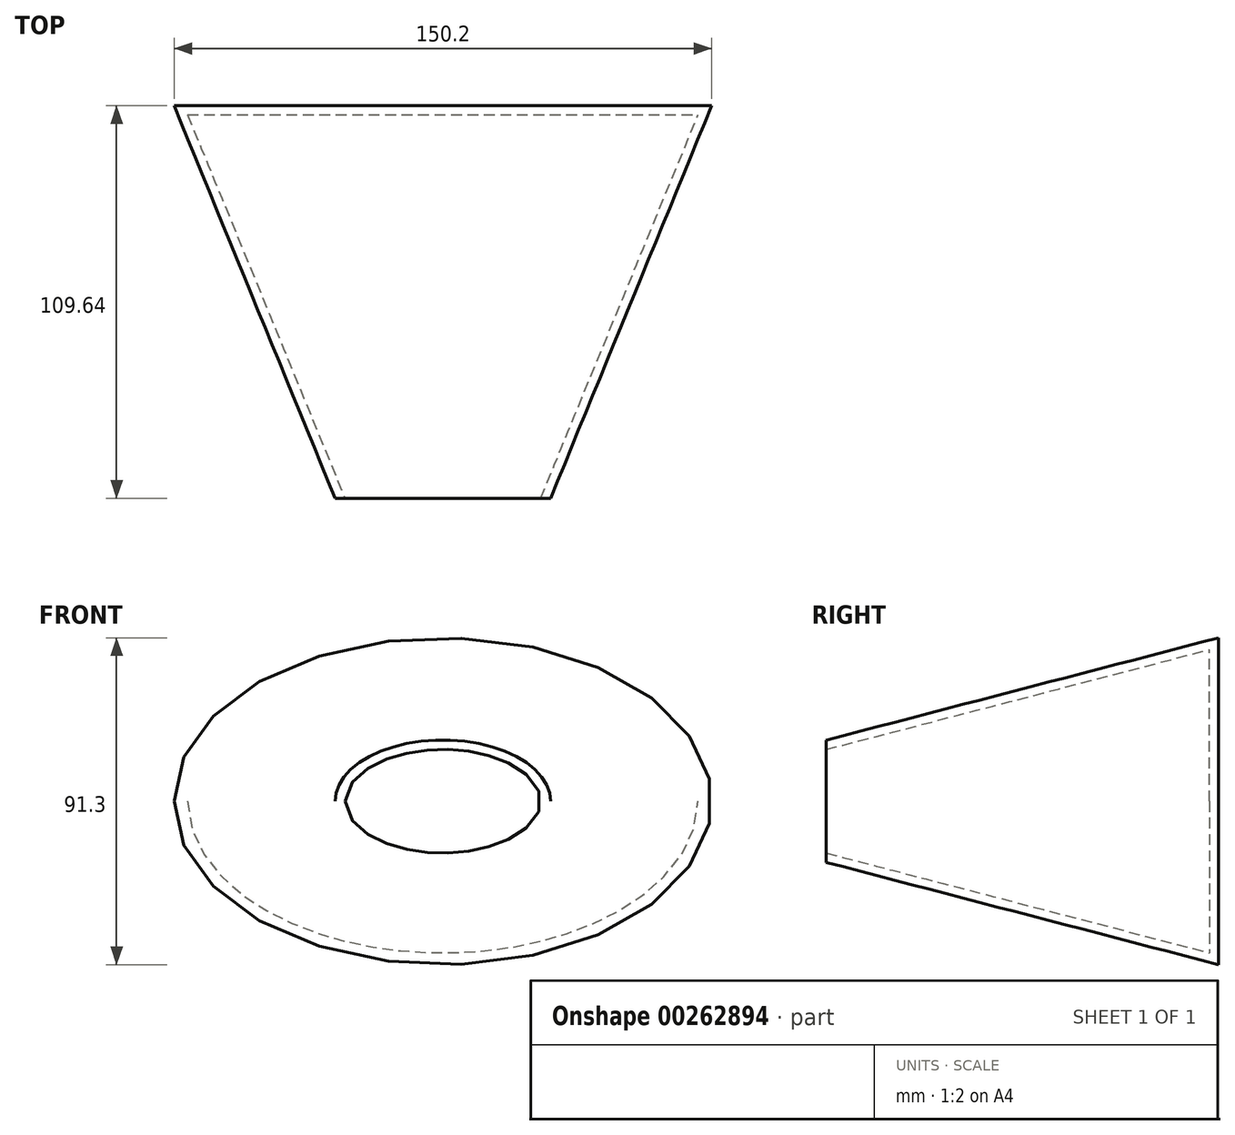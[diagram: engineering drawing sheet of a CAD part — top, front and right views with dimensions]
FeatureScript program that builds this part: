
annotation { "Feature Type Name" : "Feature", "Feature Type Description" : "" }
export const myFeature = defineFeature(function(context is Context, id is Id, definition is map)
    precondition{}
    {
        {
            var Q0;
            Q0=qCreatedBy(makeId("Front.planeOp"),FACE);
            var sketch = newSketch(context, id + "F0", { "sketchPlane" : qUnion([Q0])});
            skEllipse(sketch, "E0", {"center": v(0, 0) * mm, "majorRadius": 75.1 * mm, "minorRadius": 45.65 * mm, "majorAxis": v(-1, 0)});
            skSolve(sketch);
        }
        {
            var Q0;
            Q0=makeQuery(id+"F0.imprint","IMPRINT",FACE,{"disambiguationData":[TD([[makeQuery(id+"F0.imprint","IMPRINT",EDGE,{"derivedFrom":sQuery(id+"F0.wireOp",EDGE,"E0")}),1.0]])]});
            var sketch = newSketch(context, id + "F1", { "sketchPlane" : qUnion([Q0])});
            skEllipse(sketch, "E1", {"center": v(0, 0) * mm, "majorRadius": 30.1 * mm, "minorRadius": 17.09 * mm, "majorAxis": v(1, 0)});
            skSolve(sketch);
        }
        {
            var Q0;
            Q0 = qSketchRegion(id + "F1", true);
            extrude(context, id + "F2", {"entities" : qUnion([Q0]), "depth" : 109.64 * mm});
        }
        {
            var Q1;
            Q1=makeQuery(id+"F0.imprint","IMPRINT",FACE,{"disambiguationData":[TD([[makeQuery(id+"F0.imprint","IMPRINT",EDGE,{"derivedFrom":sQuery(id+"F0.wireOp",EDGE,"E0")}),1.0]])]});
            var Q2;
            Q2=makeQuery(id+"F2.opExtrude","CAP_FACE",FACE,{"disambiguationData":[OSD([sQuery(id+"F1.wireOp",EDGE,"E1")])],"isStart":false});
            loft(context, id + "F3", {"operationType" : NewBodyOperationType.ADD, "sheetProfilesArray" : [{ "sheetProfileEntities" : qUnion([Q1]) }, { "sheetProfileEntities" : qUnion([Q2]) }]});
        }
        {
            var Q0;
            Q0=makeQuery(id+"F2.opExtrude","CAP_FACE",FACE,{"disambiguationData":[OSD([sQuery(id+"F1.wireOp",EDGE,"E1")])],"isStart":false});
            shell(context, id + "F4", {"entities" : qUnion([Q0]), "thickness" : 2.54 * mm});
        }
    });
